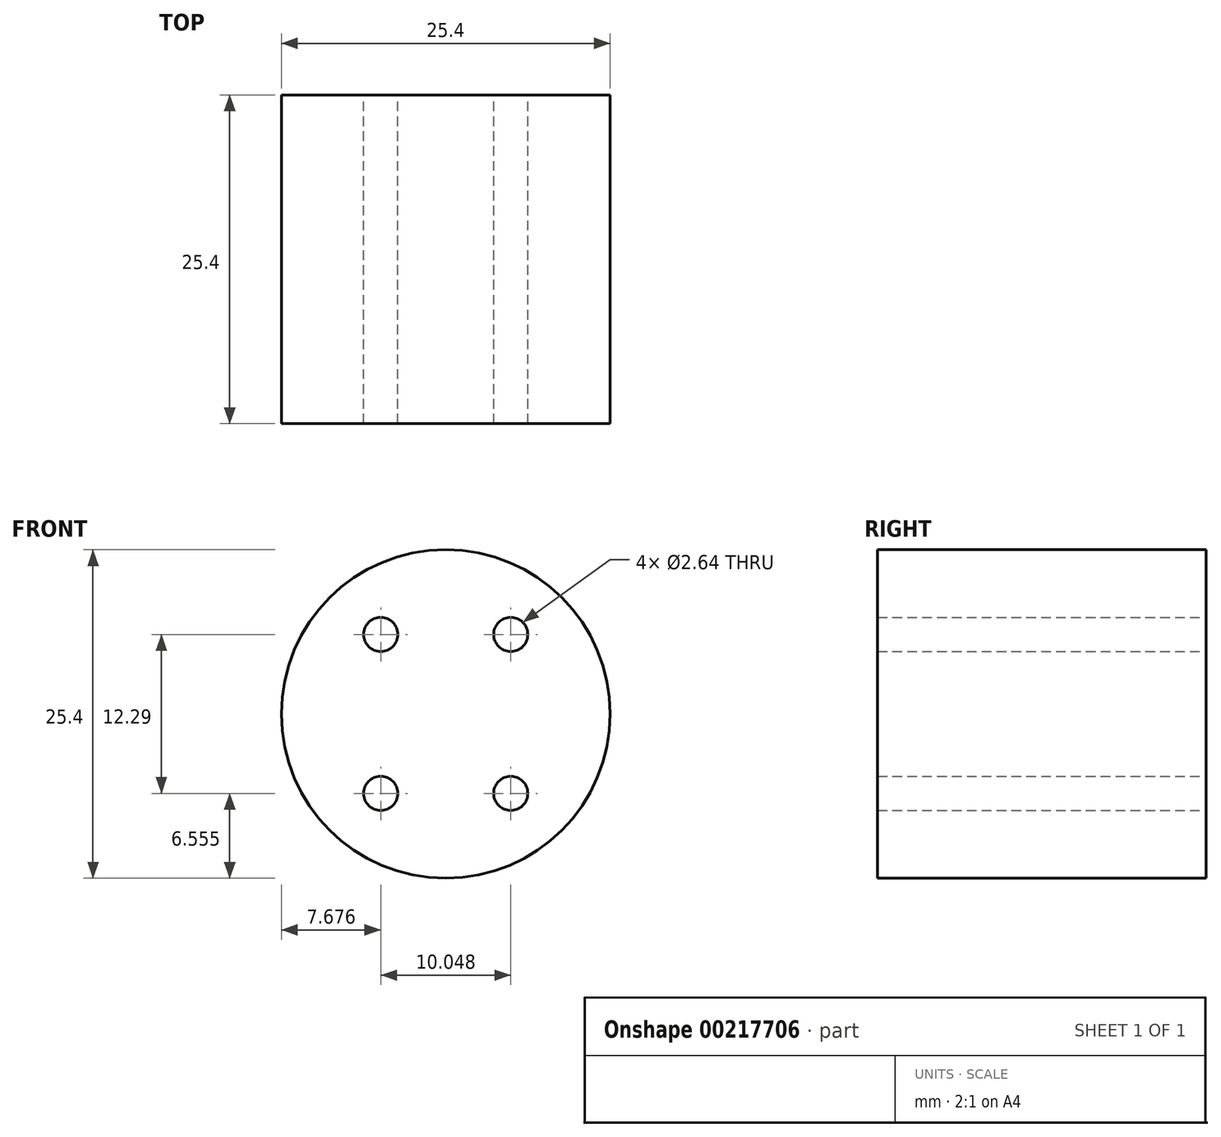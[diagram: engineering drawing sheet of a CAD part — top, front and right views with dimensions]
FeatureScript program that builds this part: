
annotation { "Feature Type Name" : "Feature", "Feature Type Description" : "" }
export const myFeature = defineFeature(function(context is Context, id is Id, definition is map)
    precondition{}
    {
        {
            var Q0;
            Q0=qCreatedBy(makeId("Front.planeOp"),FACE);
            var sketch = newSketch(context, id + "F0", { "sketchPlane" : qUnion([Q0])});
            skCircle(sketch, "E0", {"center": v(0, 0) * mm, "radius": 12.7 * mm});
            skPoint(sketch, "E1", {"position": v(-5.02, 6.15) * mm});
            skPoint(sketch, "E2", {"position": v(5.02, -6.15) * mm});
            skPoint(sketch, "E3", {"position": v(-5.02, -6.15) * mm});
            skPoint(sketch, "E4", {"position": v(5.02, 6.15) * mm});
            skCircle(sketch, "E5", {"center": v(-5.02, -6.15) * mm, "radius": 1.32 * mm});
            skCircle(sketch, "E6", {"center": v(-5.02, 6.15) * mm, "radius": 1.32 * mm});
            skCircle(sketch, "E7", {"center": v(5.02, 6.15) * mm, "radius": 1.32 * mm});
            skCircle(sketch, "E8", {"center": v(5.02, -6.15) * mm, "radius": 1.32 * mm});
            skSolve(sketch);
        }
        {
            var Q0;
            Q0 = qSketchRegion(id + "F0", true);
            extrude(context, id + "F1", {"entities" : qUnion([Q0]), "depth" : 25.4 * mm});
        }
    });
